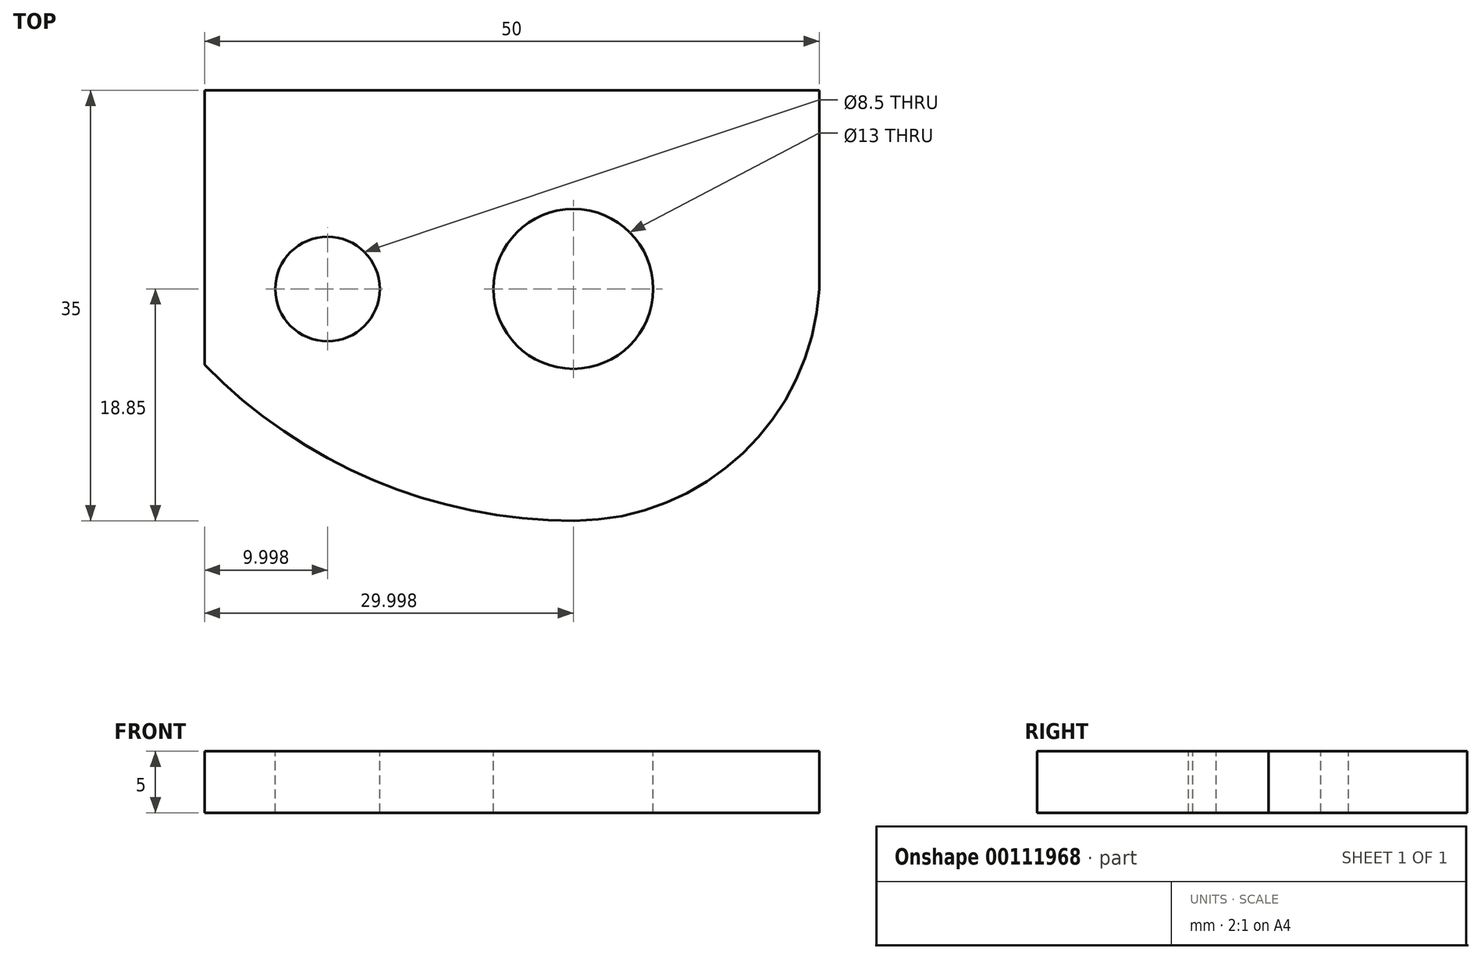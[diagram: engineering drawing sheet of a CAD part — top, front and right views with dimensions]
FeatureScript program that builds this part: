
annotation { "Feature Type Name" : "Feature", "Feature Type Description" : "" }
export const myFeature = defineFeature(function(context is Context, id is Id, definition is map)
    precondition{}
    {
        {
            var Q0;
            Q0=qCreatedBy(makeId("Top.planeOp"),FACE);
            var sketch = newSketch(context, id + "F0", { "sketchPlane" : qUnion([Q0])});
            skCircle(sketch, "E0.0", {"center": v(4.22, -2.15) * mm, "radius": 11.5 * mm});
            skCircle(sketch, "E1", {"center": v(4.22, -2.15) * mm, "radius": 6.5 * mm});
            skCircle(sketch, "E2", {"center": v(-15.78, -2.15) * mm, "radius": 4.25 * mm});
            skLineSegment(sketch, "E3", {"start": v(24.22, 14) * mm, "end": v(-25.78, 14) * mm});
            skLineSegment(sketch, "E4.bottom", {"start": v(24.22, 14) * mm, "end": v(-15.78, 14) * mm});
            skArc(sketch, "E5", {"start": v(-25.78, -8.33) * mm, "mid": v(-12.03, -17.7) * mm, "end": v(4.29, -21) * mm});
            skArc(sketch, "E6", {"start": v(4.29, -21) * mm, "mid": v(18, -15.53) * mm, "end": v(24.22, -2.15) * mm});
            skLineSegment(sketch, "E7", {"start": v(-25.78, 14) * mm, "end": v(-25.78, -8.33) * mm});
            skLineSegment(sketch, "E8", {"start": v(24.22, 14) * mm, "end": v(24.22, -2.15) * mm});
            skArc(sketch, "E9", {"start": v(-15.78, 3.85) * mm, "mid": v(-21.78, -2.15) * mm, "end": v(-15.78, -8.15) * mm});
            skArc(sketch, "E10", {"start": v(4.23, 11.85) * mm, "mid": v(-6.6, 9.93) * mm, "end": v(-15.78, 3.85) * mm});
            skArc(sketch, "E11", {"start": v(-15.78, -8.15) * mm, "mid": v(-6.6, -14.24) * mm, "end": v(4.25, -16.15) * mm});
            skArc(sketch, "E12", {"start": v(4.23, 11.85) * mm, "mid": v(18.22, -2.12) * mm, "end": v(4.29, -16.15) * mm});
            skSolve(sketch);
        }
        {
            var Q0;
            Q0=makeQuery(id+"F0.imprint","IMPRINT",FACE,{"disambiguationData":[TD([[makeQuery(id+"F0.imprint","IMPRINT",EDGE,{"derivedFrom":sQuery(id+"F0.wireOp",EDGE,"E0.0")}),-1.0]])]});
            var Q1;
            Q1=makeQuery(id+"F0.imprint","IMPRINT",FACE,{"disambiguationData":[TD([[makeQuery(id+"F0.imprint","IMPRINT",EDGE,{"derivedFrom":sQuery(id+"F0.wireOp",EDGE,"E0.0")}),1.0]])]});
            extrude(context, id + "F1", {"entities" : qUnion([Q0, Q1]), "oppositeDirection" : true, "depth" : 5 * mm});
        }
    });
